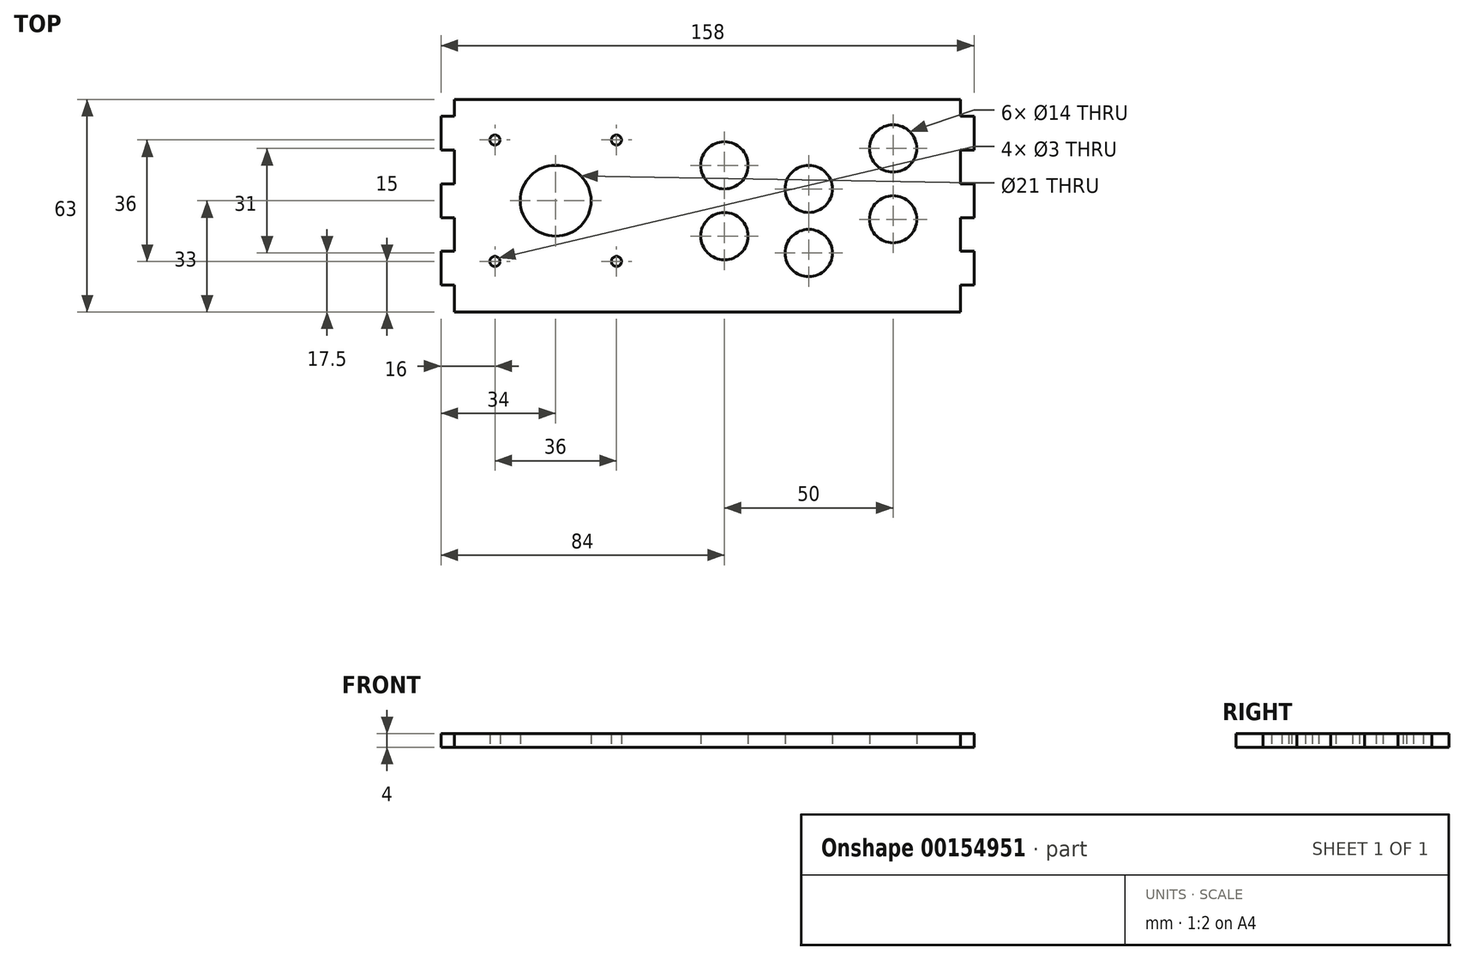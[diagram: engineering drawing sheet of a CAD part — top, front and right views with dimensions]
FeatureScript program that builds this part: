
annotation { "Feature Type Name" : "Feature", "Feature Type Description" : "" }
export const myFeature = defineFeature(function(context is Context, id is Id, definition is map)
    precondition{}
    {
        {
            var Q0;
            Q0=qCreatedBy(makeId("Top.planeOp"),FACE);
            var sketch = newSketch(context, id + "F0", { "sketchPlane" : qUnion([Q0])});
            skLineSegment(sketch, "E0.bottom", {"start": v(75, -30) * mm, "end": v(-75, -30) * mm});
            skLineSegment(sketch, "E0.top", {"start": v(75, 30) * mm, "end": v(-75, 30) * mm});
            skLineSegment(sketch, "E0.left", {"start": v(75, -30) * mm, "end": v(75, 30) * mm});
            skLineSegment(sketch, "E0.right", {"start": v(-75, -30) * mm, "end": v(-75, 30) * mm});
            skPoint(sketch, "E0.middle", {"position": v(0, 0) * mm});
            skLineSegment(sketch, "E1", {"start": v(-75, 0) * mm, "end": v(-45, 0) * mm});
            skPoint(sketch, "E1.endSnap0", {"position": v(-75, 0) * mm});
            skCircle(sketch, "E2", {"center": v(-45, 0) * mm, "radius": 10.5 * mm});
            skLineSegment(sketch, "E3", {"start": v(-45, 0) * mm, "end": v(-27, 0) * mm});
            skLineSegment(sketch, "E4", {"start": v(-27, 0) * mm, "end": v(-27, -18) * mm});
            skCircle(sketch, "E5", {"center": v(-27, -18) * mm, "radius": 1.5 * mm});
            skCircle(sketch, "E6.MirrorC", {"center": v(-27, 18) * mm, "radius": 1.5 * mm});
            skLineSegment(sketch, "E7", {"start": v(-45, 0) * mm, "end": v(-45, -5.37) * mm});
            skCircle(sketch, "E8.MirrorC", {"center": v(-63, 18) * mm, "radius": 1.5 * mm});
            skCircle(sketch, "E9.MirrorC", {"center": v(-63, -18) * mm, "radius": 1.5 * mm});
            skSolve(sketch);
        }
        {
            var Q0;
            Q0 = qSketchRegion(id + "F0", true);
            extrude(context, id + "F1", {"entities" : qUnion([Q0]), "depth" : 4 * mm});
        }
        {
            var Q0;
            Q0=makeQuery(id+"F1.opExtrude","CAP_FACE",FACE,{"disambiguationData":[OSD([sQuery(id+"F0.wireOp",EDGE,"E0.bottom"),sQuery(id+"F0.wireOp",EDGE,"E0.top"),sQuery(id+"F0.wireOp",EDGE,"E0.left"),sQuery(id+"F0.wireOp",EDGE,"E0.right"),sQuery(id+"F0.wireOp",EDGE,"E2"),sQuery(id+"F0.wireOp",EDGE,"E5"),sQuery(id+"F0.wireOp",EDGE,"E6.MirrorC"),sQuery(id+"F0.wireOp",EDGE,"E8.MirrorC"),sQuery(id+"F0.wireOp",EDGE,"E9.MirrorC")])],"isStart":true});
            var sketch = newSketch(context, id + "F2", { "sketchPlane" : qUnion([Q0])});
            skLineSegment(sketch, "E10", {"start": v(75, 0) * mm, "end": v(55, 0) * mm});
            skLineSegment(sketch, "E11", {"start": v(55, 0) * mm, "end": v(30, 0) * mm});
            skLineSegment(sketch, "E12", {"start": v(30, 0) * mm, "end": v(5, 0) * mm});
            skLineSegment(sketch, "E13", {"start": v(5, 0) * mm, "end": v(5, 10.5) * mm});
            skLineSegment(sketch, "E14", {"start": v(5, 0) * mm, "end": v(5, -10.5) * mm});
            skLineSegment(sketch, "E15", {"start": v(30, 0) * mm, "end": v(30, 15.5) * mm});
            skLineSegment(sketch, "E16", {"start": v(30, 0) * mm, "end": v(30, -3.5) * mm});
            skLineSegment(sketch, "E17", {"start": v(55, 0) * mm, "end": v(55, -15.5) * mm});
            skLineSegment(sketch, "E18", {"start": v(55, 0) * mm, "end": v(55, 5.5) * mm});
            skCircle(sketch, "E19", {"center": v(5, 10.5) * mm, "radius": 7 * mm});
            skCircle(sketch, "E20", {"center": v(5, -10.5) * mm, "radius": 7 * mm});
            skCircle(sketch, "E21", {"center": v(30, 15.5) * mm, "radius": 7 * mm});
            skCircle(sketch, "E22", {"center": v(30, -3.5) * mm, "radius": 7 * mm});
            skCircle(sketch, "E23", {"center": v(55, 5.5) * mm, "radius": 7 * mm});
            skCircle(sketch, "E24", {"center": v(55, -15.5) * mm, "radius": 7 * mm});
            skSolve(sketch);
        }
        {
            var Q0;
            Q0 = qSketchRegion(id + "F2", true);
            extrude(context, id + "F3", {"entities" : qUnion([Q0]), "operationType" : NewBodyOperationType.REMOVE, "oppositeDirection" : true, "depth" : 25 * mm});
        }
        {
            var Q0;
            Q0=makeQuery(id+"F1.opExtrude","CAP_FACE",FACE,{"disambiguationData":[OSD([sQuery(id+"F0.wireOp",EDGE,"E0.bottom"),sQuery(id+"F0.wireOp",EDGE,"E0.top"),sQuery(id+"F0.wireOp",EDGE,"E0.left"),sQuery(id+"F0.wireOp",EDGE,"E0.right"),sQuery(id+"F0.wireOp",EDGE,"E2"),sQuery(id+"F0.wireOp",EDGE,"E5"),sQuery(id+"F0.wireOp",EDGE,"E6.MirrorC"),sQuery(id+"F0.wireOp",EDGE,"E8.MirrorC"),sQuery(id+"F0.wireOp",EDGE,"E9.MirrorC")])],"isStart":true});
            var sketch = newSketch(context, id + "F4", { "sketchPlane" : qUnion([Q0])});
            skLineSegment(sketch, "E25", {"start": v(-75, 0) * mm, "end": v(-75, 5) * mm});
            skLineSegment(sketch, "E26", {"start": v(-75, 5) * mm, "end": v(-79, 5) * mm});
            skLineSegment(sketch, "E27", {"start": v(-79, 5) * mm, "end": v(-79, -5) * mm});
            skLineSegment(sketch, "E28", {"start": v(-79, -5) * mm, "end": v(-75, -5) * mm});
            skLineSegment(sketch, "E29", {"start": v(-75, -5) * mm, "end": v(-75, 0) * mm});
            skLineSegment(sketch, "E30.0.1.0", {"start": v(-75, 25) * mm, "end": v(-79, 25) * mm});
            skLineSegment(sketch, "E30.0.1.1", {"start": v(-79, 25) * mm, "end": v(-79, 15) * mm});
            skLineSegment(sketch, "E30.0.1.2", {"start": v(-75, 20) * mm, "end": v(-75, 25) * mm});
            skLineSegment(sketch, "E30.0.1.3", {"start": v(-75, 15) * mm, "end": v(-75, 20) * mm});
            skLineSegment(sketch, "E30.0.1.4", {"start": v(-79, 15) * mm, "end": v(-75, 15) * mm});
            skLineSegment(sketch, "E30.direction1", {"start": v(-79, 5) * mm, "end": v(-54, 5) * mm, "construction": true});
            skLineSegment(sketch, "E30.direction2", {"start": v(-79, 5) * mm, "end": v(-79, 25) * mm, "construction": true});
            skLineSegment(sketch, "E31.0.1.0", {"start": v(-79, -15) * mm, "end": v(-54, -15) * mm, "construction": true});
            skLineSegment(sketch, "E31.0.1.1", {"start": v(-79, -15) * mm, "end": v(-79, -25) * mm});
            skLineSegment(sketch, "E31.0.1.2", {"start": v(-79, -25) * mm, "end": v(-75, -25) * mm});
            skLineSegment(sketch, "E31.0.1.3", {"start": v(-75, -25) * mm, "end": v(-75, -20) * mm});
            skLineSegment(sketch, "E31.0.1.4", {"start": v(-75, -20) * mm, "end": v(-75, -15) * mm});
            skLineSegment(sketch, "E31.direction2", {"start": v(-79, 5) * mm, "end": v(-79, -15) * mm, "construction": true});
            skLineSegment(sketch, "E32", {"start": v(-79, -15) * mm, "end": v(-75, -15) * mm});
            skLineSegment(sketch, "E33", {"start": v(0, 30) * mm, "end": v(0, 25.9) * mm});
            skLineSegment(sketch, "E34.MirrorCS", {"start": v(75, 5) * mm, "end": v(79, 5) * mm});
            skLineSegment(sketch, "E35.MirrorCS", {"start": v(79, -15) * mm, "end": v(75, -15) * mm});
            skLineSegment(sketch, "E36.MirrorCS", {"start": v(79, 5) * mm, "end": v(54, 5) * mm, "construction": true});
            skLineSegment(sketch, "E37.MirrorCS", {"start": v(79, -15) * mm, "end": v(54, -15) * mm, "construction": true});
            skLineSegment(sketch, "E38.MirrorCS", {"start": v(79, 15) * mm, "end": v(75, 15) * mm});
            skLineSegment(sketch, "E39.MirrorCS", {"start": v(75, 25) * mm, "end": v(79, 25) * mm});
            skLineSegment(sketch, "E40.MirrorCS", {"start": v(79, -5) * mm, "end": v(75, -5) * mm});
            skLineSegment(sketch, "E41.MirrorCS", {"start": v(79, -25) * mm, "end": v(75, -25) * mm});
            skLineSegment(sketch, "E42.MirrorCS", {"start": v(79, -15) * mm, "end": v(79, -25) * mm});
            skLineSegment(sketch, "E43.MirrorCS", {"start": v(79, 5) * mm, "end": v(79, -15) * mm, "construction": true});
            skLineSegment(sketch, "E44.MirrorCS", {"start": v(79, 5) * mm, "end": v(79, 25) * mm, "construction": true});
            skLineSegment(sketch, "E45", {"start": v(75, 25) * mm, "end": v(75, 15) * mm});
            skLineSegment(sketch, "E46", {"start": v(79, 25) * mm, "end": v(79, 15) * mm});
            skLineSegment(sketch, "E47", {"start": v(79, 5) * mm, "end": v(79, -5) * mm});
            skLineSegment(sketch, "E48", {"start": v(75, 5) * mm, "end": v(75, -5) * mm});
            skLineSegment(sketch, "E49", {"start": v(75, -15) * mm, "end": v(75, -25) * mm});
            skLineSegment(sketch, "E50", {"start": v(-75, 30) * mm, "end": v(-75, 33) * mm});
            skLineSegment(sketch, "E51", {"start": v(-75, 33) * mm, "end": v(75, 33) * mm});
            skLineSegment(sketch, "E52", {"start": v(75, 33) * mm, "end": v(75, 30) * mm});
            skLineSegment(sketch, "E53", {"start": v(75, 30) * mm, "end": v(-75, 30) * mm});
            skSolve(sketch);
        }
        {
            var Q0;
            Q0 = qSketchRegion(id + "F4", true);
            var Q1;
            Q1=makeQuery(id+"F1.opExtrude","CAP_FACE",FACE,{"disambiguationData":[OSD([sQuery(id+"F0.wireOp",EDGE,"E0.bottom"),sQuery(id+"F0.wireOp",EDGE,"E0.top"),sQuery(id+"F0.wireOp",EDGE,"E0.left"),sQuery(id+"F0.wireOp",EDGE,"E0.right"),sQuery(id+"F0.wireOp",EDGE,"E2"),sQuery(id+"F0.wireOp",EDGE,"E5"),sQuery(id+"F0.wireOp",EDGE,"E6.MirrorC"),sQuery(id+"F0.wireOp",EDGE,"E8.MirrorC"),sQuery(id+"F0.wireOp",EDGE,"E9.MirrorC")])],"isStart":false});
            extrude(context, id + "F5", {"entities" : qUnion([Q0]), "operationType" : NewBodyOperationType.ADD, "oppositeDirection" : true, "endBoundEntityFace" : qUnion([Q1]), "depth" : 4 * mm});
        }
    });
